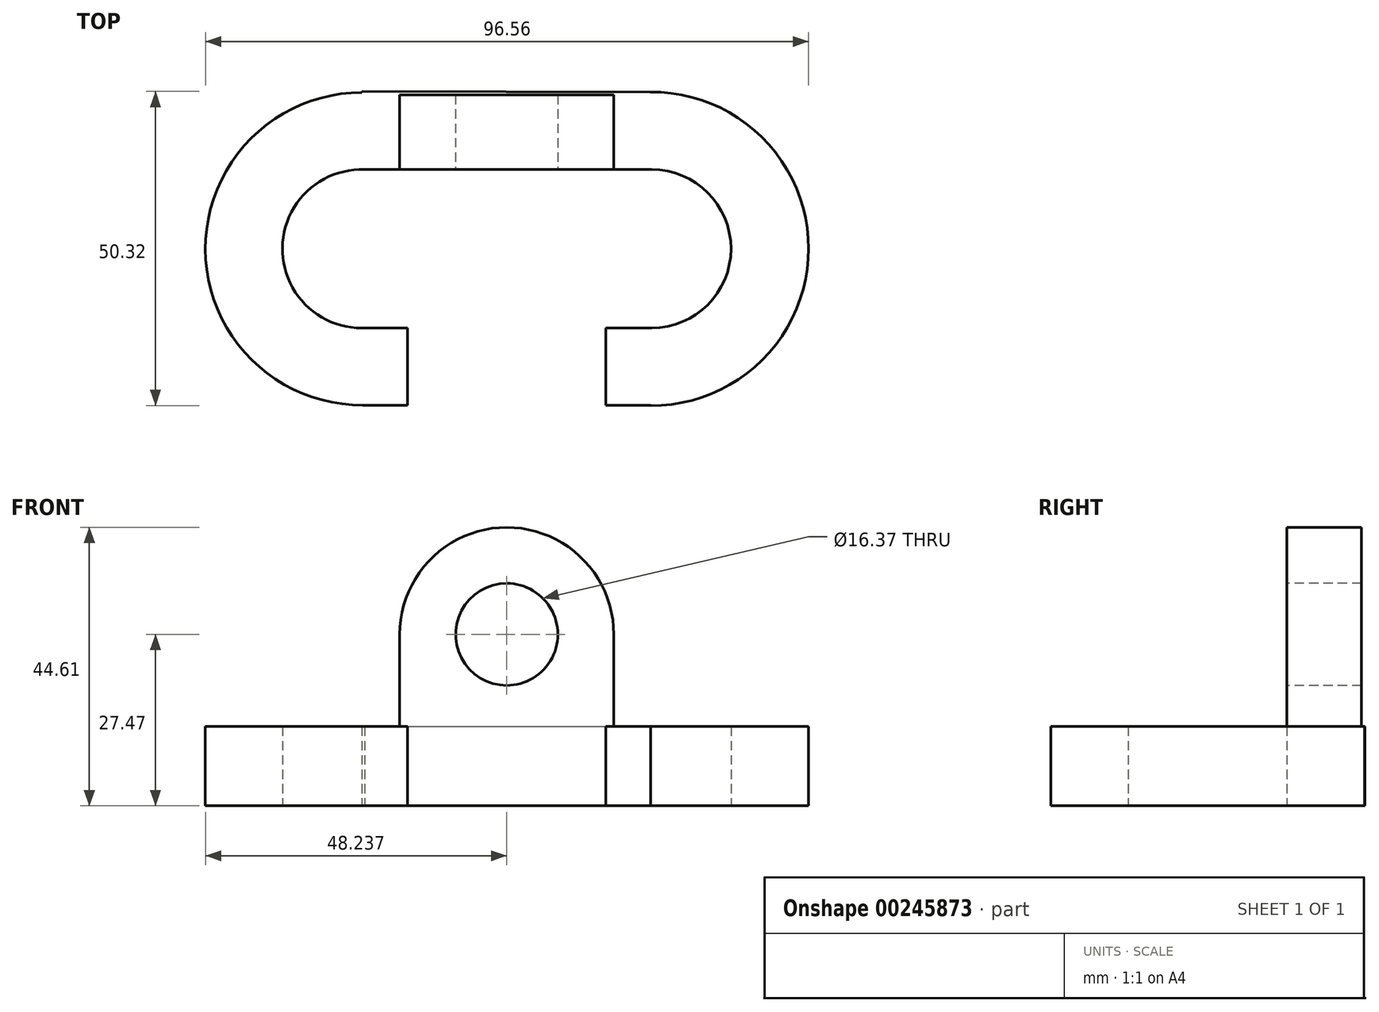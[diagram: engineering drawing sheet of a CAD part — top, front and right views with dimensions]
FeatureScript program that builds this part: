
annotation { "Feature Type Name" : "Feature", "Feature Type Description" : "" }
export const myFeature = defineFeature(function(context is Context, id is Id, definition is map)
    precondition{}
    {
        {
            var Q0;
            Q0=qCreatedBy(makeId("Top.planeOp"),FACE);
            var sketch = newSketch(context, id + "F0", { "sketchPlane" : qUnion([Q0])});
            skArc(sketch, "E0", {"start": v(23.2, -12.7) * mm, "mid": v(35.9, 0.21) * mm, "end": v(22.77, 12.7) * mm});
            skPoint(sketch, "E1.trimOffspring.end.orphan", {"position": v(0, 12.3) * mm});
            skLineSegment(sketch, "E2", {"start": v(23.2, 12.7) * mm, "end": v(22.77, 12.7) * mm});
            skPoint(sketch, "E3.end.orphan", {"position": v(0, -25.32) * mm});
            skLineSegment(sketch, "E4", {"start": v(23.07, -25.04) * mm, "end": v(23.06, -25.4) * mm});
            skArc(sketch, "E5.MirrorCS", {"start": v(-23.2, -12.7) * mm, "mid": v(-35.9, 0.21) * mm, "end": v(-22.77, 12.7) * mm});
            skPoint(sketch, "E6.MirrorCS.start.orphan", {"position": v(-23.06, -25.4) * mm});
            skArc(sketch, "E7", {"start": v(23.07, -25.12) * mm, "mid": v(48.32, 0.04) * mm, "end": v(23, 25.12) * mm});
            skLineSegment(sketch, "E8", {"start": v(23.2, 12.7) * mm, "end": v(23, 25.12) * mm});
            skLineSegment(sketch, "E9", {"start": v(-23.2, 12.7) * mm, "end": v(-23.2, 25.2) * mm});
            skArc(sketch, "E10", {"start": v(-23.2, 25.04) * mm, "mid": v(-48.24, -0.07) * mm, "end": v(-23.07, -25.04) * mm});
            skLineSegment(sketch, "E11", {"start": v(-23.2, 25.2) * mm, "end": v(23, 25.12) * mm});
            skLineSegment(sketch, "E12", {"start": v(-22.77, 12.7) * mm, "end": v(23.2, 12.7) * mm});
            skLineSegment(sketch, "E13", {"start": v(-15.88, -12.7) * mm, "end": v(-23.2, -12.7) * mm});
            skLineSegment(sketch, "E14", {"start": v(-23.07, -25.04) * mm, "end": v(-15.88, -25.04) * mm});
            skLineSegment(sketch, "E15", {"start": v(-15.88, -25.04) * mm, "end": v(-15.88, -12.7) * mm});
            skLineSegment(sketch, "E16.MirrorCS", {"start": v(15.88, -12.7) * mm, "end": v(23.2, -12.7) * mm});
            skLineSegment(sketch, "E17.MirrorCS", {"start": v(23.07, -25.04) * mm, "end": v(15.88, -25.04) * mm});
            skLineSegment(sketch, "E18.MirrorCS", {"start": v(15.88, -25.04) * mm, "end": v(15.88, -12.7) * mm});
            skPoint(sketch, "E19.orphan", {"position": v(13.37, -12.7) * mm});
            skPoint(sketch, "E20.end.orphan", {"position": v(-13.37, -12.7) * mm});
            skSolve(sketch);
        }
        {
            var Q0;
            {var subQ5=sQuery(id+"F0.wireOp",EDGE,"E10");Q0=makeQuery(id+"F0.imprint","IMPRINT",FACE,{"disambiguationData":[TD([[makeQuery(id+"F0.imprint","IMPRINT",EDGE,{"derivedFrom":subQ5}),1.0]])]});}
            var Q1;
            {var subQ5=sQuery(id+"F0.wireOp",EDGE,"E8");Q1=makeQuery(id+"F0.imprint","IMPRINT",FACE,{"disambiguationData":[TD([[makeQuery(id+"F0.imprint","IMPRINT",EDGE,{"derivedFrom":subQ5}),1.0]])]});}
            var Q2;
            {var subQ4=sQuery(id+"F0.wireOp",EDGE,"E7");Q2=makeQuery(id+"F0.imprint","IMPRINT",FACE,{"disambiguationData":[TD([[makeQuery(id+"F0.imprint","IMPRINT",EDGE,{"derivedFrom":subQ4}),1.0]])]});}
            extrude(context, id + "F1", {"entities" : qUnion([Q0, Q1, Q2]), "depth" : 12.7 * mm});
        }
        {
            var Q0;
            Q0=makeQuery(id+"F1.opExtrude","SWEPT_FACE",FACE,{"disambiguationData":[OSD([sQuery(id+"F0.wireOp",EDGE,"E12")])]});
            var sketch = newSketch(context, id + "F2", { "sketchPlane" : qUnion([Q0])});
            skCircle(sketch, "E21", {"center": v(0, 27.47) * mm, "radius": 8.18 * mm});
            skArc(sketch, "E22", {"start": v(17.14, 27.47) * mm, "mid": v(0, 44.6) * mm, "end": v(-17.14, 27.47) * mm});
            skLineSegment(sketch, "E23", {"start": v(0, 27.47) * mm, "end": v(17.14, 27.47) * mm, "construction": true});
            skLineSegment(sketch, "E24", {"start": v(0, 27.47) * mm, "end": v(-17.14, 27.47) * mm, "construction": true});
            skLineSegment(sketch, "E25", {"start": v(-17.14, 12.7) * mm, "end": v(17.14, 12.7) * mm});
            skLineSegment(sketch, "E26", {"start": v(-17.14, 27.47) * mm, "end": v(-17.14, 12.7) * mm});
            skLineSegment(sketch, "E27", {"start": v(17.14, 27.47) * mm, "end": v(17.14, 12.7) * mm});
            skSolve(sketch);
        }
        {
            var Q0;
            Q0 = qSketchRegion(id + "F2", true);
            extrude(context, id + "F3", {"entities" : qUnion([Q0]), "operationType" : NewBodyOperationType.ADD, "oppositeDirection" : true, "depth" : 11.94 * mm});
        }
    });
